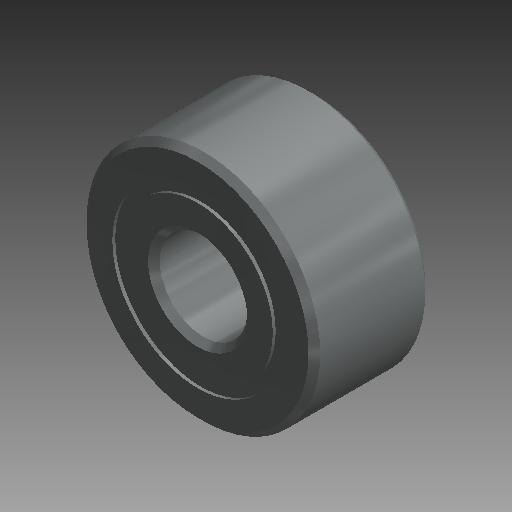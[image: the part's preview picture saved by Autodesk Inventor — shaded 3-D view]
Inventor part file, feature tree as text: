
AUTODESK INVENTOR PART (.ipt)
format: ipt  version: 2019 (Build 230136000, 136)  size: 573,440 bytes
history: native  units: mm (DEFAULTED — no unit token found)
features: other x11, revolve x5
ambient origin geometry x8: Origin, YZ Plane, XZ Plane, XY Plane, X Axis, Y Axis, Z Axis, Center Point
bodies: Solid1 (feature_tree), Solid2 (feature_tree), Solid3 (feature_tree), Solid4 (feature_tree), Solid5 (feature_tree), Solid6 (feature_tree), Solid7 (feature_tree), Solid8 (feature_tree), Solid9 (feature_tree), Solid10 (feature_tree), Solid11 (feature_tree), Solid12 (feature_tree), Solid13 (feature_tree), Solid14 (feature_tree), Solid15 (feature_tree), Solid16 (feature_tree)
feature tree (16):
  revolve  "Revolve1"  [1 undecoded]
  revolve  "Revolve3"  [1 undecoded]
  revolve  "Revolve4"  [1 undecoded]
  other  "CirPattern1[1]"
  other  "CirPattern1[2]"
  other  "CirPattern1[3]"
  other  "CirPattern1[4]"
  other  "CirPattern1[5]"
  other  "CirPattern1[6]"
  other  "CirPattern1[7]"
  other  "CirPattern1[8]"
  other  "CirPattern1[9]"
  other  "CirPattern1[10]"
  other  "CirPattern1[11]"
  revolve  "Revolve5[1]"  [1 undecoded]
  revolve  "Revolve5[2]"  [1 undecoded]
note: 5 required parameter values undecoded (feature->parameter linkage not recoverable at this tier; creation-order binding heuristic only, values carry confidence <= 0.55)
